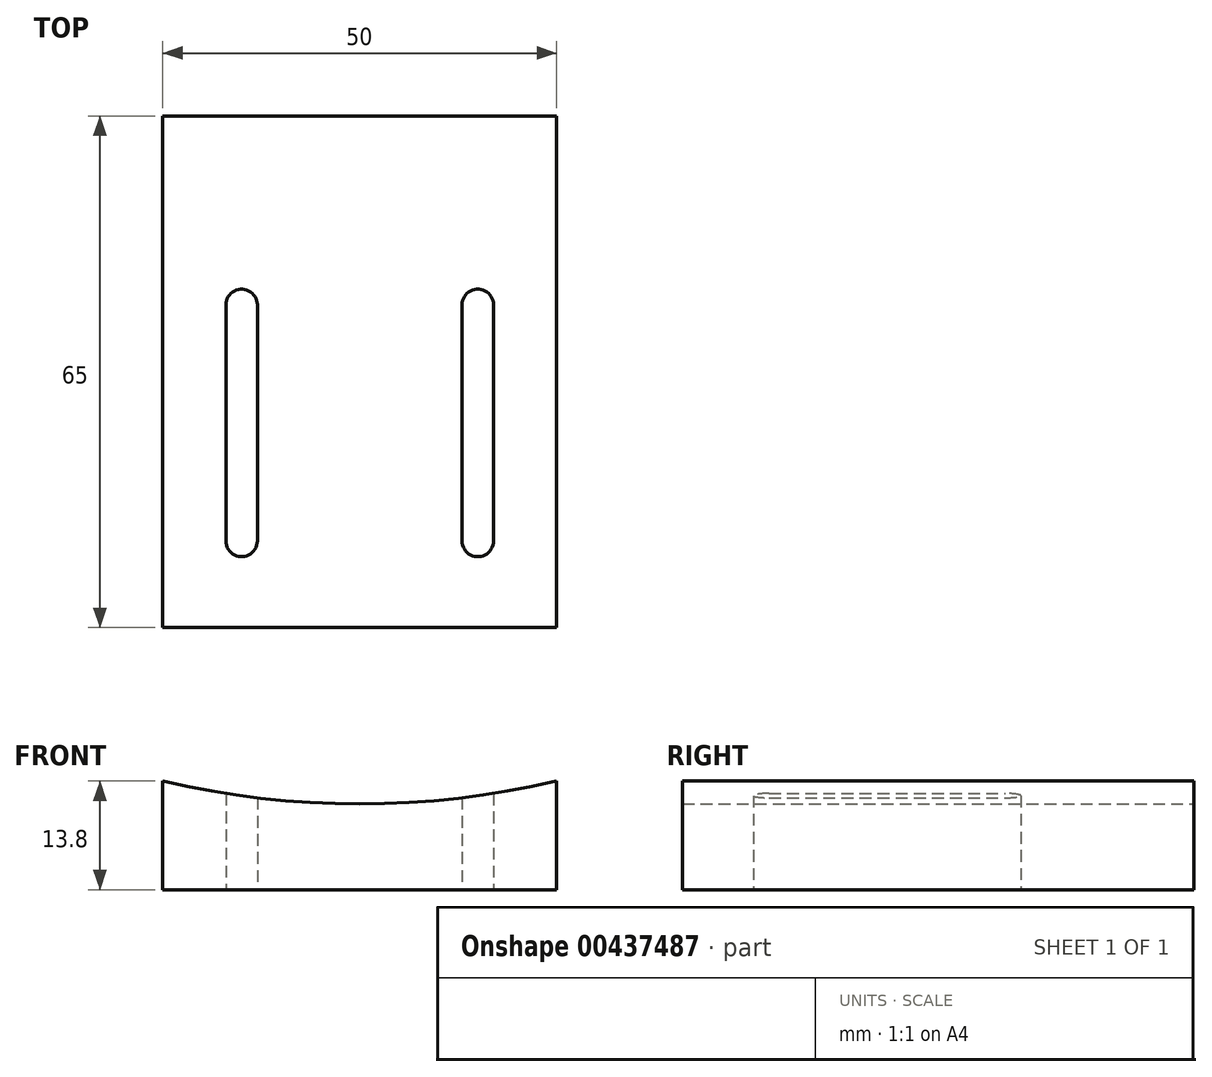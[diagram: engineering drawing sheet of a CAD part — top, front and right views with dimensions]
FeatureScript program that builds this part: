
annotation { "Feature Type Name" : "Feature", "Feature Type Description" : "" }
export const myFeature = defineFeature(function(context is Context, id is Id, definition is map)
    precondition{}
    {
        {
            var Q0;
            Q0=qCreatedBy(makeId("Top.planeOp"),FACE);
            var sketch = newSketch(context, id + "F0", { "sketchPlane" : qUnion([Q0])});
            skLineSegment(sketch, "E0.bottom", {"start": v(-25, 32.5) * mm, "end": v(25, 32.5) * mm});
            skLineSegment(sketch, "E0.top", {"start": v(-25, -32.5) * mm, "end": v(25, -32.5) * mm});
            skLineSegment(sketch, "E0.left", {"start": v(-25, 32.5) * mm, "end": v(-25, -32.5) * mm});
            skLineSegment(sketch, "E0.right", {"start": v(25, 32.5) * mm, "end": v(25, -32.5) * mm});
            skSolve(sketch);
        }
        {
            var Q0;
            Q0 = qSketchRegion(id + "F0", true);
            extrude(context, id + "F1", {"entities" : qUnion([Q0]), "depth" : 13.8 * mm});
        }
        {
            var Q0;
            Q0=makeQuery(id+"F1.opExtrude","SWEPT_FACE",FACE,{"disambiguationData":[OSD([sQuery(id+"F0.wireOp",EDGE,"E0.bottom")])]});
            var sketch = newSketch(context, id + "F2", { "sketchPlane" : qUnion([Q0])});
            skCircle(sketch, "E1", {"center": v(0, 119.9) * mm, "radius": 109 * mm});
            skPoint(sketch, "E1.first.point", {"position": v(25, 13.8) * mm});
            skPoint(sketch, "E1.second.point", {"position": v(-25, 13.8) * mm});
            skPoint(sketch, "E1.third.point", {"position": v(0, 10.9) * mm});
            skSolve(sketch);
        }
        {
            var Q0;
            Q0 = qSketchRegion(id + "F2", true);
            extrude(context, id + "F3", {"entities" : qUnion([Q0]), "operationType" : NewBodyOperationType.REMOVE, "oppositeDirection" : true, "depth" : 65 * mm});
        }
        {
            var Q0;
            Q0=makeQuery(id+"F1.opExtrude","CAP_FACE",FACE,{"disambiguationData":[OSD([sQuery(id+"F0.wireOp",EDGE,"E0.bottom"),sQuery(id+"F0.wireOp",EDGE,"E0.top"),sQuery(id+"F0.wireOp",EDGE,"E0.left"),sQuery(id+"F0.wireOp",EDGE,"E0.right")])],"isStart":true});
            var sketch = newSketch(context, id + "F4", { "sketchPlane" : qUnion([Q0])});
            skLineSegment(sketch, "E2.bottom", {"start": v(-13, 21.5) * mm, "end": v(-17, 21.5) * mm});
            skLineSegment(sketch, "E2.top", {"start": v(-13, -8.5) * mm, "end": v(-17, -8.5) * mm});
            skLineSegment(sketch, "E2.left", {"start": v(-13, 21.5) * mm, "end": v(-13, -8.5) * mm});
            skLineSegment(sketch, "E2.right", {"start": v(-17, 21.5) * mm, "end": v(-17, -8.5) * mm});
            skLineSegment(sketch, "E3.bottom", {"start": v(13, 21.5) * mm, "end": v(17, 21.5) * mm});
            skLineSegment(sketch, "E3.top", {"start": v(13, -8.5) * mm, "end": v(17, -8.5) * mm});
            skLineSegment(sketch, "E3.left", {"start": v(13, 21.5) * mm, "end": v(13, -8.5) * mm});
            skLineSegment(sketch, "E3.right", {"start": v(17, 21.5) * mm, "end": v(17, -8.5) * mm});
            skCircle(sketch, "E4", {"center": v(-15, 21.5) * mm, "radius": 2 * mm});
            skPoint(sketch, "E4.third.point", {"position": v(-15, 23.5) * mm});
            skPoint(sketch, "E4.third.point.positionSnap0", {"position": v(-15, 21.5) * mm});
            skCircle(sketch, "E5", {"center": v(15, 21.5) * mm, "radius": 2 * mm});
            skPoint(sketch, "E5.third.point", {"position": v(15, 23.5) * mm});
            skPoint(sketch, "E5.third.point.positionSnap0", {"position": v(15, 21.5) * mm});
            skCircle(sketch, "E6", {"center": v(-15, -8.5) * mm, "radius": 2 * mm});
            skPoint(sketch, "E6.third.point", {"position": v(-13.7, -6.98) * mm});
            skCircle(sketch, "E7", {"center": v(15, -8.5) * mm, "radius": 2 * mm});
            skPoint(sketch, "E7.third.point", {"position": v(15.62, -6.6) * mm});
            skSolve(sketch);
        }
        {
            var Q0;
            Q0 = qSketchRegion(id + "F4", true);
            extrude(context, id + "F5", {"entities" : qUnion([Q0]), "operationType" : NewBodyOperationType.REMOVE, "oppositeDirection" : true, "depth" : 15 * mm});
        }
    });
